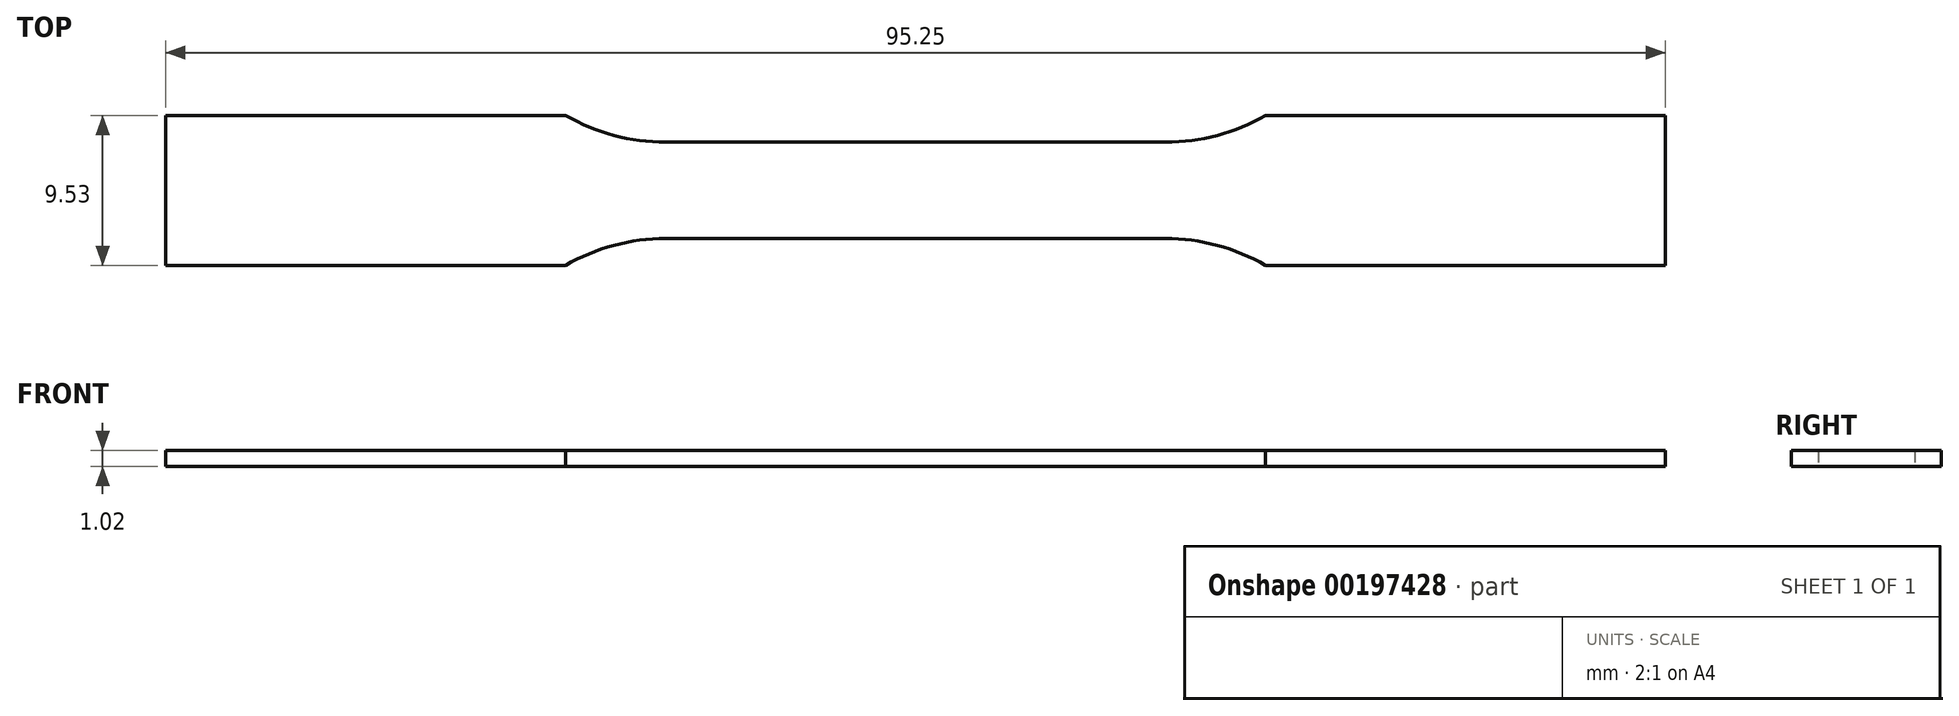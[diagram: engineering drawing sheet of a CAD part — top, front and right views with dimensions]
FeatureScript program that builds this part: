
annotation { "Feature Type Name" : "Feature", "Feature Type Description" : "" }
export const myFeature = defineFeature(function(context is Context, id is Id, definition is map)
    precondition{}
    {
        {
            var Q0;
            Q0=qCreatedBy(makeId("Top.planeOp"),FACE);
            var sketch = newSketch(context, id + "F0", { "sketchPlane" : qUnion([Q0])});
            skLineSegment(sketch, "E0.bottom", {"start": v(15.88, 3.06) * mm, "end": v(-15.87, 3.06) * mm});
            skLineSegment(sketch, "E0.top", {"start": v(15.87, -3.06) * mm, "end": v(-15.88, -3.06) * mm});
            skPoint(sketch, "E0.middle", {"position": v(0, 0) * mm});
            skArc(sketch, "E1", {"start": v(15.88, 3.06) * mm, "mid": v(19.16, 3.5) * mm, "end": v(22.22, 4.76) * mm});
            skArc(sketch, "E2", {"start": v(22.22, -4.77) * mm, "mid": v(19.16, -3.5) * mm, "end": v(15.87, -3.06) * mm});
            skLineSegment(sketch, "E3", {"start": v(22.22, 4.76) * mm, "end": v(47.62, 4.76) * mm});
            skLineSegment(sketch, "E4", {"start": v(47.62, 4.76) * mm, "end": v(47.62, -4.77) * mm});
            skLineSegment(sketch, "E5", {"start": v(47.62, -4.77) * mm, "end": v(22.22, -4.77) * mm});
            skLineSegment(sketch, "E6.MirrorCS", {"start": v(-47.61, 4.76) * mm, "end": v(-47.63, -4.77) * mm});
            skLineSegment(sketch, "E7.MirrorCS", {"start": v(-47.63, -4.77) * mm, "end": v(-22.24, -4.77) * mm});
            skLineSegment(sketch, "E8.MirrorCS", {"start": v(-22.21, 4.76) * mm, "end": v(-47.61, 4.76) * mm});
            skArc(sketch, "E9.MirrorCS", {"start": v(-15.87, 3.06) * mm, "mid": v(-19.15, 3.5) * mm, "end": v(-22.21, 4.76) * mm});
            skArc(sketch, "E10.MirrorCS", {"start": v(-22.24, -4.77) * mm, "mid": v(-19.17, -3.5) * mm, "end": v(-15.88, -3.06) * mm});
            skSolve(sketch);
        }
        {
            var Q0;
            Q0=makeQuery(id+"F0.imprint","IMPRINT",FACE,{"disambiguationData":[TD([[makeQuery(id+"F0.imprint","IMPRINT",EDGE,{"derivedFrom":sQuery(id+"F0.wireOp",EDGE,"E0.bottom")}),1.0]])]});
            extrude(context, id + "F1", {"entities" : qUnion([Q0]), "depth" : 1.02 * mm});
        }
    });
